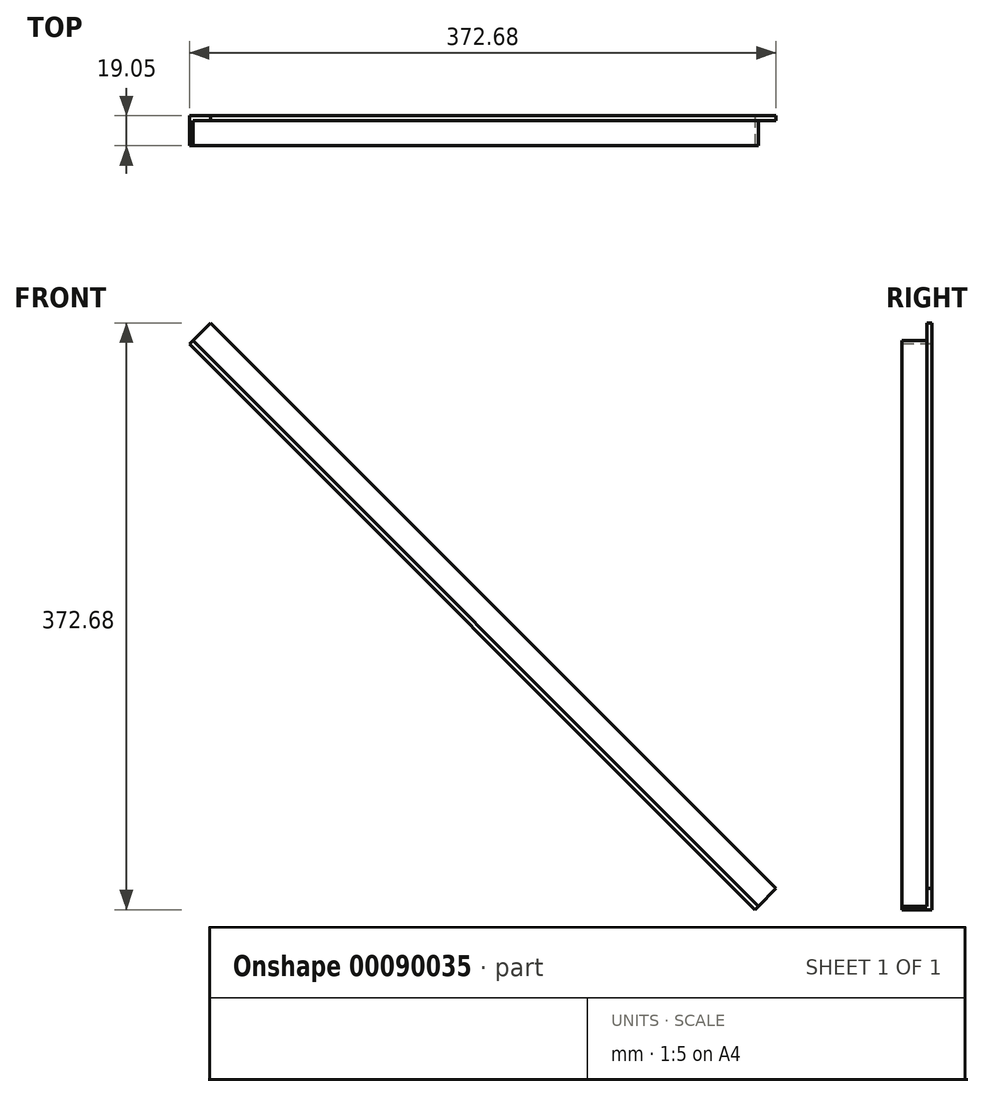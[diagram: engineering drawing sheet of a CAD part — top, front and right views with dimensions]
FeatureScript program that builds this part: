
annotation { "Feature Type Name" : "Feature", "Feature Type Description" : "" }
export const myFeature = defineFeature(function(context is Context, id is Id, definition is map)
    precondition{}
    {
        {
            var Q0;
            Q0=qCreatedBy(makeId("Front.planeOp"),FACE);
            var sketch = newSketch(context, id + "F0", { "sketchPlane" : qUnion([Q0])});
            skLineSegment(sketch, "E0", {"start": v(0, 0) * mm, "end": v(179.6, 179.6) * mm});
            skLineSegment(sketch, "E1", {"start": v(0, 0) * mm, "end": v(0, 78.9) * mm});
            skLineSegment(sketch, "E2", {"start": v(0, 78.9) * mm, "end": v(179.6, 179.6) * mm});
            skSolve(sketch);
        }
        {
            var Q0;
            Q0=sQuery(id+"F0.wireOp",EDGE,"E0");
            var Q1;
            Q1=qCreatedBy(makeId("Top.planeOp"),FACE);
            cPlane(context, id + "F1", {"entities" : qUnion([Q0, Q1]), "cplaneType" : CPlaneType.LINE_ANGLE, "offset" : 152.4 * mm, "angle" : 0 * degree, "width" : 152.4 * mm, "height" : 152.4 * mm});
        }
        {
            var Q0;
            Q0=qCreatedBy(id+"F1.planeOp",FACE);
            var sketch = newSketch(context, id + "F2", { "sketchPlane" : qUnion([Q0])});
            skLineSegment(sketch, "E3", {"start": v(0, 0) * mm, "end": v(0, 19.05) * mm});
            skLineSegment(sketch, "E4", {"start": v(0, 0) * mm, "end": v(-19.05, 0) * mm});
            skLineSegment(sketch, "E5.0", {"start": v(-3.17, 3.18) * mm, "end": v(-19.05, 3.17) * mm});
            skLineSegment(sketch, "E5.1", {"start": v(-3.17, 3.18) * mm, "end": v(-3.17, 19.05) * mm});
            skLineSegment(sketch, "E6", {"start": v(0, 19.05) * mm, "end": v(-3.17, 19.05) * mm});
            skLineSegment(sketch, "E7", {"start": v(-19.05, 3.17) * mm, "end": v(-19.05, 0) * mm});
            skSolve(sketch);
        }
        {
            var Q0;
            Q0 = qSketchRegion(id + "F2", true);
            extrude(context, id + "F3", {"entities" : qUnion([Q0]), "depth" : 508 * mm});
        }
    });
